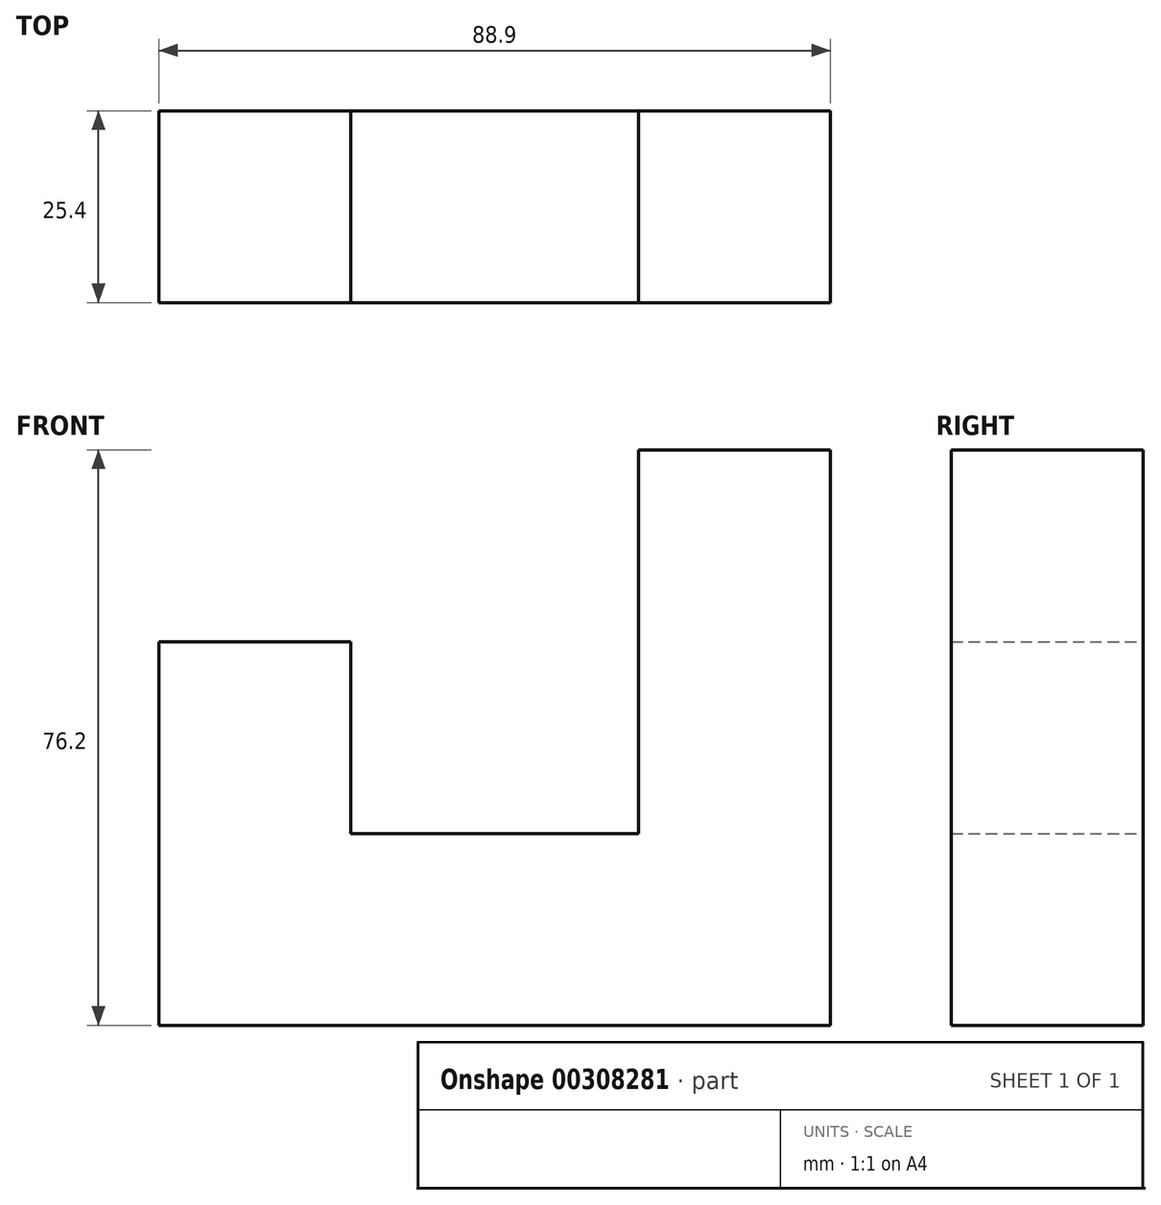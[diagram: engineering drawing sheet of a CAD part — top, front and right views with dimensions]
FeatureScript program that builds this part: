
annotation { "Feature Type Name" : "Feature", "Feature Type Description" : "" }
export const myFeature = defineFeature(function(context is Context, id is Id, definition is map)
    precondition{}
    {
        {
            var Q0;
            Q0=qCreatedBy(makeId("Front.planeOp"),FACE);
            var sketch = newSketch(context, id + "F0", { "sketchPlane" : qUnion([Q0])});
            skLineSegment(sketch, "E0", {"start": v(-46.79, -28.57) * mm, "end": v(-46.79, 22.23) * mm});
            skLineSegment(sketch, "E1", {"start": v(-46.79, 22.23) * mm, "end": v(-21.39, 22.23) * mm});
            skLineSegment(sketch, "E2", {"start": v(-21.39, 22.23) * mm, "end": v(-21.39, -3.17) * mm});
            skLineSegment(sketch, "E3", {"start": v(-21.39, -3.17) * mm, "end": v(16.71, -3.17) * mm});
            skLineSegment(sketch, "E4", {"start": v(16.71, -3.17) * mm, "end": v(16.71, 47.63) * mm});
            skLineSegment(sketch, "E5", {"start": v(16.71, 47.63) * mm, "end": v(42.11, 47.63) * mm});
            skLineSegment(sketch, "E6", {"start": v(42.11, 47.63) * mm, "end": v(42.11, -28.57) * mm});
            skLineSegment(sketch, "E7", {"start": v(42.11, -28.57) * mm, "end": v(-46.79, -28.57) * mm});
            skSolve(sketch);
        }
        {
            var Q0;
            Q0 = qSketchRegion(id + "F0", true);
            extrude(context, id + "F1", {"entities" : qUnion([Q0]), "depth" : 25.4 * mm});
        }
    });
